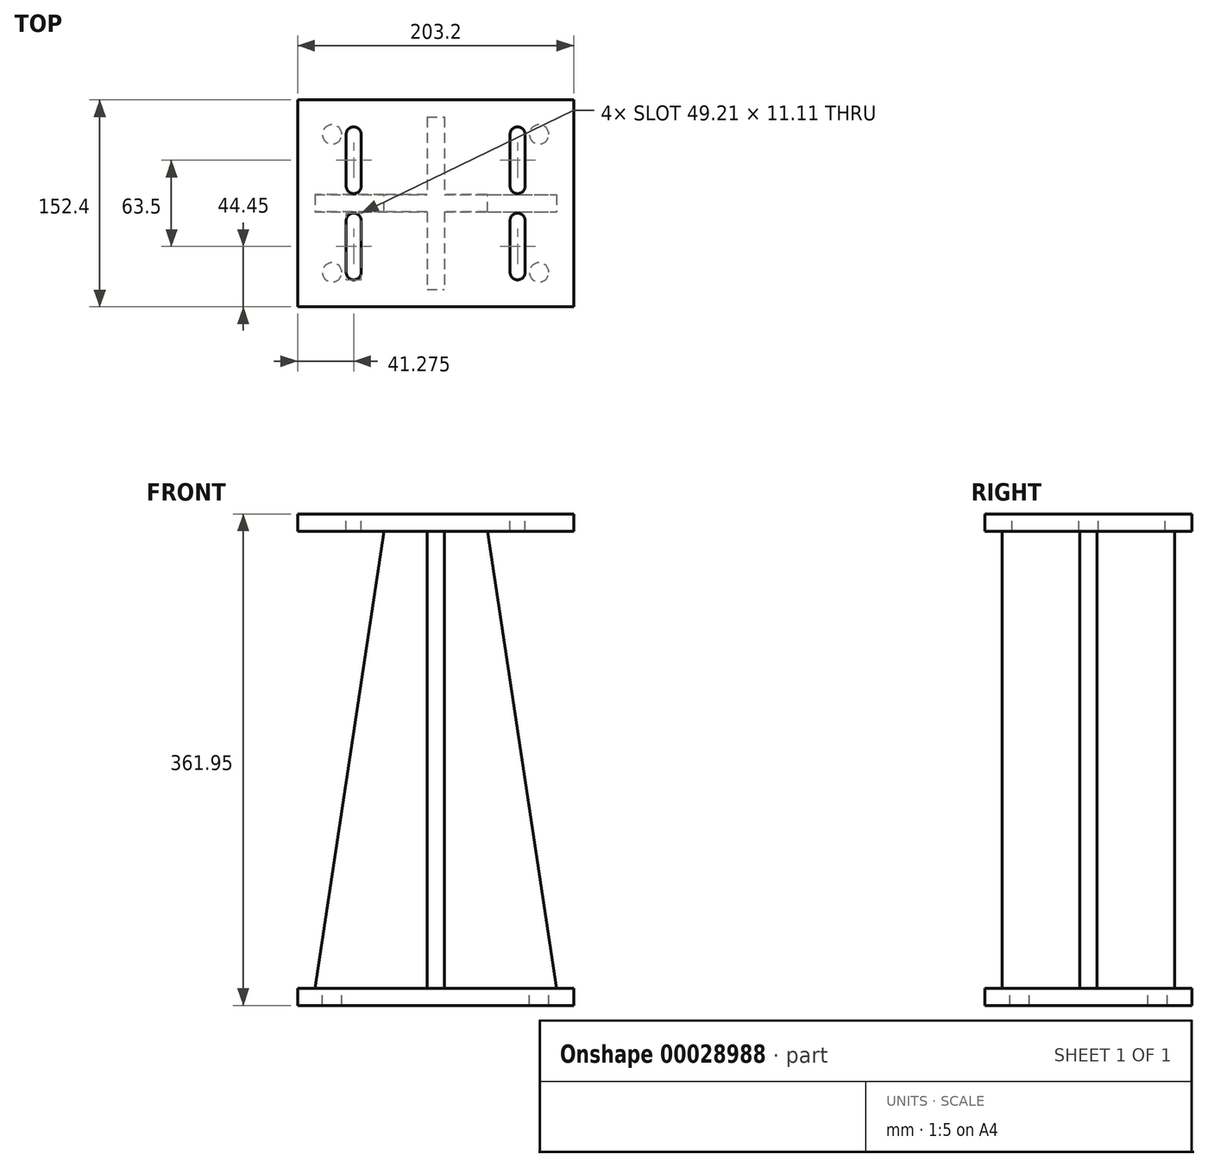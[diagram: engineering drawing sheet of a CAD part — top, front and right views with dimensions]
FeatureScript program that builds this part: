
annotation { "Feature Type Name" : "Feature", "Feature Type Description" : "" }
export const myFeature = defineFeature(function(context is Context, id is Id, definition is map)
    precondition{}
    {
        {
            var Q0;
            Q0=qCreatedBy(makeId("Top.planeOp"),FACE);
            var sketch = newSketch(context, id + "F0", { "sketchPlane" : qUnion([Q0])});
            skLineSegment(sketch, "E0.rect.bottom", {"start": v(-101.6, 76.2) * mm, "end": v(101.6, 76.2) * mm});
            skLineSegment(sketch, "E0.rect.top", {"start": v(-101.6, -76.2) * mm, "end": v(101.6, -76.2) * mm});
            skLineSegment(sketch, "E0.rect.left", {"start": v(-101.6, 76.2) * mm, "end": v(-101.6, -76.2) * mm});
            skLineSegment(sketch, "E0.rect.right", {"start": v(101.6, 76.2) * mm, "end": v(101.6, -76.2) * mm});
            skPoint(sketch, "E0.rect.middle", {"position": v(0, 0) * mm});
            skLineSegment(sketch, "E1.0", {"start": v(-76.2, 50.8) * mm, "end": v(76.2, 50.8) * mm, "construction": true});
            skLineSegment(sketch, "E1.1", {"start": v(-76.2, 50.8) * mm, "end": v(-76.2, -50.8) * mm, "construction": true});
            skLineSegment(sketch, "E1.2", {"start": v(-76.2, -50.8) * mm, "end": v(76.2, -50.8) * mm, "construction": true});
            skLineSegment(sketch, "E1.3", {"start": v(76.2, 50.8) * mm, "end": v(76.2, -50.8) * mm, "construction": true});
            skPoint(sketch, "E2", {"position": v(-76.2, 50.8) * mm});
            skPoint(sketch, "E3", {"position": v(76.2, 50.8) * mm});
            skPoint(sketch, "E4", {"position": v(76.2, -50.8) * mm});
            skPoint(sketch, "E5", {"position": v(-76.2, -50.8) * mm});
            skSolve(sketch);
        }
        {
            var Q0;
            Q0 = qSketchRegion(id + "F0", true);
            extrude(context, id + "F1", {"entities" : qUnion([Q0]), "oppositeDirection" : true, "depth" : 12.7 * mm});
        }
        {
            var Q0;
            Q0=sQuery(id+"F0.wireOp",VERTEX,"E2");
            var Q1;
            Q1=sQuery(id+"F0.wireOp",VERTEX,"E3");
            var Q2;
            Q2=sQuery(id+"F0.wireOp",VERTEX,"E4");
            var Q3;
            Q3=sQuery(id+"F0.wireOp",VERTEX,"E5");
            var Q4;
            Q4=makeQuery(id+"F1.opExtrude","SWEPT_BODY",BODY,{"disambiguationData":[OSD([sQuery(id+"F0.wireOp",EDGE,"E0.rect.bottom"),sQuery(id+"F0.wireOp",EDGE,"E0.rect.top"),sQuery(id+"F0.wireOp",EDGE,"E0.rect.left"),sQuery(id+"F0.wireOp",EDGE,"E0.rect.right")])]});
            hole(context, id + "F2", {"style" : HoleStyle.SIMPLE, "holeDiameter" : 14.22 * mm, "endStyle" : HoleEndStyle.THROUGH, "locations" : qUnion([Q0, Q1, Q2, Q3]), "scope" : qUnion([Q4])});
        }
        {
            var Q0;
            Q0=makeQuery(id+"F1.opExtrude","CAP_FACE",FACE,{"disambiguationData":[OSD([sQuery(id+"F0.wireOp",EDGE,"E0.rect.bottom"),sQuery(id+"F0.wireOp",EDGE,"E0.rect.top"),sQuery(id+"F0.wireOp",EDGE,"E0.rect.left"),sQuery(id+"F0.wireOp",EDGE,"E0.rect.right")])],"isStart":false});
            cPlane(context, id + "F3", {"entities" : qUnion([Q0]), "cplaneType" : CPlaneType.OFFSET, "offset" : 361.95 * mm, "oppositeDirection" : true, "width" : 152.4 * mm, "height" : 152.4 * mm});
        }
        {
            var Q0;
            Q0=qCreatedBy(id+"F3.planeOp",FACE);
            var sketch = newSketch(context, id + "F4", { "sketchPlane" : qUnion([Q0])});
            skLineSegment(sketch, "E6.0", {"start": v(-101.6, -76.2) * mm, "end": v(101.6, -76.2) * mm});
            skLineSegment(sketch, "E7.0", {"start": v(101.6, -76.2) * mm, "end": v(101.6, 76.2) * mm});
            skLineSegment(sketch, "E8.0", {"start": v(-101.6, 76.2) * mm, "end": v(101.6, 76.2) * mm});
            skLineSegment(sketch, "E9.0", {"start": v(-101.6, -76.2) * mm, "end": v(-101.6, 76.2) * mm});
            skSolve(sketch);
        }
        {
            var Q0;
            Q0 = qSketchRegion(id + "F4", true);
            extrude(context, id + "F5", {"entities" : qUnion([Q0]), "depth" : 12.7 * mm});
        }
        {
            var Q0;
            Q0=makeQuery(id+"F0.imprint","IMPRINT",FACE,{"disambiguationData":[TD([[makeQuery(id+"F0.imprint","IMPRINT",EDGE,{"derivedFrom":sQuery(id+"F0.wireOp",EDGE,"E0.rect.bottom")}),-1.0]])]});
            var sketch = newSketch(context, id + "F6", { "sketchPlane" : qUnion([Q0])});
            skLineSegment(sketch, "E10.rect.bottom", {"start": v(-6.35, 63.5) * mm, "end": v(6.35, 63.5) * mm});
            skLineSegment(sketch, "E10.rect.top", {"start": v(-6.35, -63.5) * mm, "end": v(6.35, -63.5) * mm});
            skLineSegment(sketch, "E10.rect.left", {"start": v(-6.35, 63.5) * mm, "end": v(-6.35, -63.5) * mm});
            skLineSegment(sketch, "E10.rect.right", {"start": v(6.35, 63.5) * mm, "end": v(6.35, -63.5) * mm});
            skPoint(sketch, "E10.rect.middle", {"position": v(0, 0) * mm});
            skLineSegment(sketch, "E11.rect.bottom", {"start": v(-38.1, 6.35) * mm, "end": v(38.1, 6.35) * mm});
            skLineSegment(sketch, "E11.rect.top", {"start": v(-38.1, -6.35) * mm, "end": v(38.1, -6.35) * mm});
            skLineSegment(sketch, "E11.rect.left", {"start": v(-38.1, 6.35) * mm, "end": v(-38.1, -6.35) * mm});
            skLineSegment(sketch, "E11.rect.right", {"start": v(38.1, 6.35) * mm, "end": v(38.1, -6.35) * mm});
            skSolve(sketch);
        }
        {
            var Q0;
            Q0 = qSketchRegion(id + "F6", true);
            var Q1;
            Q1=makeQuery(id+"F5.opExtrude","CAP_FACE",FACE,{"disambiguationData":[OSD([sQuery(id+"F4.wireOp",EDGE,"E6.0"),sQuery(id+"F4.wireOp",EDGE,"E7.0"),sQuery(id+"F4.wireOp",EDGE,"E8.0"),sQuery(id+"F4.wireOp",EDGE,"E9.0")])],"isStart":false});
            extrude(context, id + "F7", {"entities" : qUnion([Q0]), "endBound" : BoundingType.UP_TO_SURFACE, "endBoundEntityFace" : qUnion([Q1]), "depth" : 25.4 * mm});
        }
        {
            var Q0;
            Q0=makeQuery(id+"F5.opExtrude","CAP_FACE",FACE,{"disambiguationData":[OSD([sQuery(id+"F4.wireOp",EDGE,"E6.0"),sQuery(id+"F4.wireOp",EDGE,"E7.0"),sQuery(id+"F4.wireOp",EDGE,"E8.0"),sQuery(id+"F4.wireOp",EDGE,"E9.0")])],"isStart":true});
            var sketch = newSketch(context, id + "F8", { "sketchPlane" : qUnion([Q0])});
            skLineSegment(sketch, "E12", {"start": v(-101.6, 0) * mm, "end": v(101.6, 0) * mm, "construction": true});
            skLineSegment(sketch, "E13", {"start": v(0, 76.2) * mm, "end": v(0, -76.2) * mm, "construction": true});
            skLineSegment(sketch, "E14.0", {"start": v(-60.32, 76.2) * mm, "end": v(-60.33, -76.2) * mm, "construction": true});
            skLineSegment(sketch, "E15.0", {"start": v(-101.6, 19.81) * mm, "end": v(101.6, 19.81) * mm, "construction": true});
            skPoint(sketch, "E16", {"position": v(-60.32, 19.81) * mm});
            skPoint(sketch, "E17.MirrorP", {"position": v(-60.32, -19.81) * mm});
            skPoint(sketch, "E18.MirrorP", {"position": v(60.32, 19.81) * mm});
            skPoint(sketch, "E19.MirrorP", {"position": v(60.32, -19.81) * mm});
            skLineSegment(sketch, "E20", {"start": v(-60.32, 12.7) * mm, "end": v(-60.32, 50.8) * mm});
            skArc(sketch, "E21.0.startCap", {"start": v(-54.77, 12.7) * mm, "mid": v(-60.32, 7.14) * mm, "end": v(-65.88, 12.7) * mm});
            skArc(sketch, "E21.0.endCap", {"start": v(-65.88, 50.8) * mm, "mid": v(-60.32, 56.36) * mm, "end": v(-54.77, 50.8) * mm});
            skLineSegment(sketch, "E21.0.left", {"start": v(-65.88, 12.7) * mm, "end": v(-65.88, 50.8) * mm});
            skLineSegment(sketch, "E21.0.right", {"start": v(-54.77, 12.7) * mm, "end": v(-54.77, 50.8) * mm});
            skLineSegment(sketch, "E22.MirrorCS", {"start": v(-65.88, -12.7) * mm, "end": v(-65.88, -50.8) * mm});
            skLineSegment(sketch, "E23.MirrorCS", {"start": v(-54.77, -12.7) * mm, "end": v(-54.77, -50.8) * mm});
            skLineSegment(sketch, "E24.MirrorCS", {"start": v(-60.32, -12.7) * mm, "end": v(-60.32, -50.8) * mm});
            skArc(sketch, "E25.MirrorCS", {"start": v(-65.88, -50.8) * mm, "mid": v(-60.32, -56.36) * mm, "end": v(-54.77, -50.8) * mm});
            skArc(sketch, "E26.MirrorCS", {"start": v(-54.77, -12.7) * mm, "mid": v(-60.32, -7.14) * mm, "end": v(-65.88, -12.7) * mm});
            skArc(sketch, "E27.MirrorCS", {"start": v(54.77, -12.7) * mm, "mid": v(60.32, -7.14) * mm, "end": v(65.88, -12.7) * mm});
            skArc(sketch, "E28.MirrorCS", {"start": v(54.77, 12.7) * mm, "mid": v(60.33, 7.14) * mm, "end": v(65.88, 12.7) * mm});
            skLineSegment(sketch, "E29.MirrorCS", {"start": v(65.88, -12.7) * mm, "end": v(65.88, -50.8) * mm});
            skLineSegment(sketch, "E30.MirrorCS", {"start": v(60.32, 12.7) * mm, "end": v(60.33, 50.8) * mm});
            skArc(sketch, "E31.MirrorCS", {"start": v(65.88, -50.8) * mm, "mid": v(60.32, -56.36) * mm, "end": v(54.77, -50.8) * mm});
            skLineSegment(sketch, "E32.MirrorCS", {"start": v(54.77, -12.7) * mm, "end": v(54.77, -50.8) * mm});
            skLineSegment(sketch, "E33.MirrorCS", {"start": v(60.32, -12.7) * mm, "end": v(60.32, -50.8) * mm});
            skArc(sketch, "E34.MirrorCS", {"start": v(65.88, 50.8) * mm, "mid": v(60.33, 56.36) * mm, "end": v(54.77, 50.8) * mm});
            skLineSegment(sketch, "E35.MirrorCS", {"start": v(65.88, 12.7) * mm, "end": v(65.88, 50.8) * mm});
            skLineSegment(sketch, "E36.MirrorCS", {"start": v(54.77, 12.7) * mm, "end": v(54.77, 50.8) * mm});
            skSolve(sketch);
        }
        {
            var Q0;
            Q0 = qSketchRegion(id + "F8", true);
            extrude(context, id + "F9", {"entities" : qUnion([Q0]), "operationType" : NewBodyOperationType.REMOVE, "oppositeDirection" : true, "depth" : 25.4 * mm});
        }
        {
            var Q0;
            {var subQ0=sQuery(id+"F6.wireOp",EDGE,"E11.rect.top");Q0=makeQuery(id+"F7.opExtrude","SWEPT_FACE",FACE,{"disambiguationData":[OSD([subQ0]),TDD([makeQuery(id+"F6.imprint","IMPRINT",EDGE,{"disambiguationData":[TD([[makeQuery(id+"F6.imprint","INTERSECT",VERTEX,{"derivedFrom":[subQ0,sQuery(id+"F6.wireOp",EDGE,"E11.rect.right")]}),1.0]])],"derivedFrom":subQ0})])]});}
            var sketch = newSketch(context, id + "F10", { "sketchPlane" : qUnion([Q0])});
            skLineSegment(sketch, "E37.0", {"start": v(38.1, 336.55) * mm, "end": v(38.1, 0) * mm});
            skLineSegment(sketch, "E38.0", {"start": v(-101.6, 0) * mm, "end": v(101.6, 0) * mm});
            skLineSegment(sketch, "E39", {"start": v(38.1, 336.55) * mm, "end": v(88.9, 0) * mm});
            skLineSegment(sketch, "E40", {"start": v(0, 353.21) * mm, "end": v(0, -98.5) * mm, "construction": true});
            skLineSegment(sketch, "E41.MirrorCS", {"start": v(-38.1, 336.55) * mm, "end": v(-38.1, 0) * mm});
            skLineSegment(sketch, "E42.MirrorCS", {"start": v(-38.1, 336.55) * mm, "end": v(-88.9, 0) * mm});
            skSolve(sketch);
        }
        {
            var Q0;
            Q0 = qSketchRegion(id + "F10", true);
            extrude(context, id + "F11", {"entities" : qUnion([Q0]), "operationType" : NewBodyOperationType.ADD, "oppositeDirection" : true, "depth" : 12.7 * mm});
        }
    });
